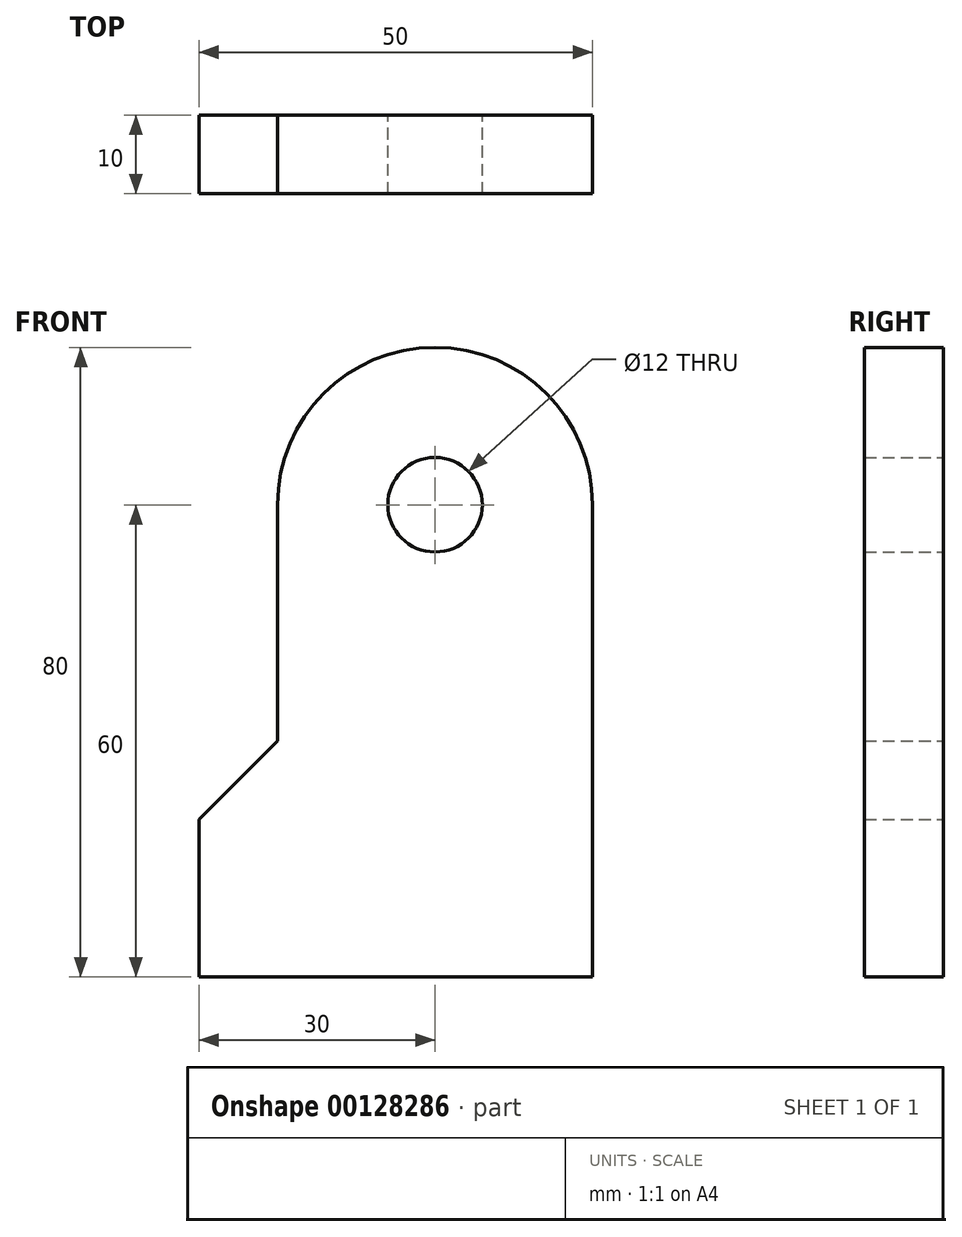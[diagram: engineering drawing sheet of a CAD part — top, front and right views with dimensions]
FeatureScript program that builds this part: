
annotation { "Feature Type Name" : "Feature", "Feature Type Description" : "" }
export const myFeature = defineFeature(function(context is Context, id is Id, definition is map)
    precondition{}
    {
        {
            var Q0;
            Q0=qCreatedBy(makeId("Front.planeOp"),FACE);
            var sketch = newSketch(context, id + "F0", { "sketchPlane" : qUnion([Q0])});
            skCircle(sketch, "E0", {"center": v(0, 0) * mm, "radius": 6 * mm});
            skLineSegment(sketch, "E1", {"start": v(-20, 0) * mm, "end": v(-20, -30) * mm});
            skLineSegment(sketch, "E2", {"start": v(-20, -30) * mm, "end": v(-30, -40) * mm});
            skLineSegment(sketch, "E3", {"start": v(-30, -40) * mm, "end": v(-30, -60) * mm});
            skLineSegment(sketch, "E4", {"start": v(-30, -60) * mm, "end": v(20, -60) * mm});
            skLineSegment(sketch, "E5", {"start": v(20, -60) * mm, "end": v(20, 0) * mm});
            skLineSegment(sketch, "E6", {"start": v(0, 20) * mm, "end": v(0, 20) * mm});
            skPoint(sketch, "E7.visualSharp", {"position": v(-20, 20) * mm});
            skArc(sketch, "E7.filletArc", {"start": v(0, 20) * mm, "mid": v(-14.14, 14.14) * mm, "end": v(-20, 0) * mm});
            skPoint(sketch, "E8.visualSharp", {"position": v(20, 20) * mm});
            skArc(sketch, "E8.filletArc", {"start": v(20, 0) * mm, "mid": v(14.14, 14.14) * mm, "end": v(0, 20) * mm});
            skSolve(sketch);
        }
        {
            var Q0;
            Q0 = qSketchRegion(id + "F0", true);
            extrude(context, id + "F1", {"entities" : qUnion([Q0]), "depth" : 10 * mm});
        }
    });
